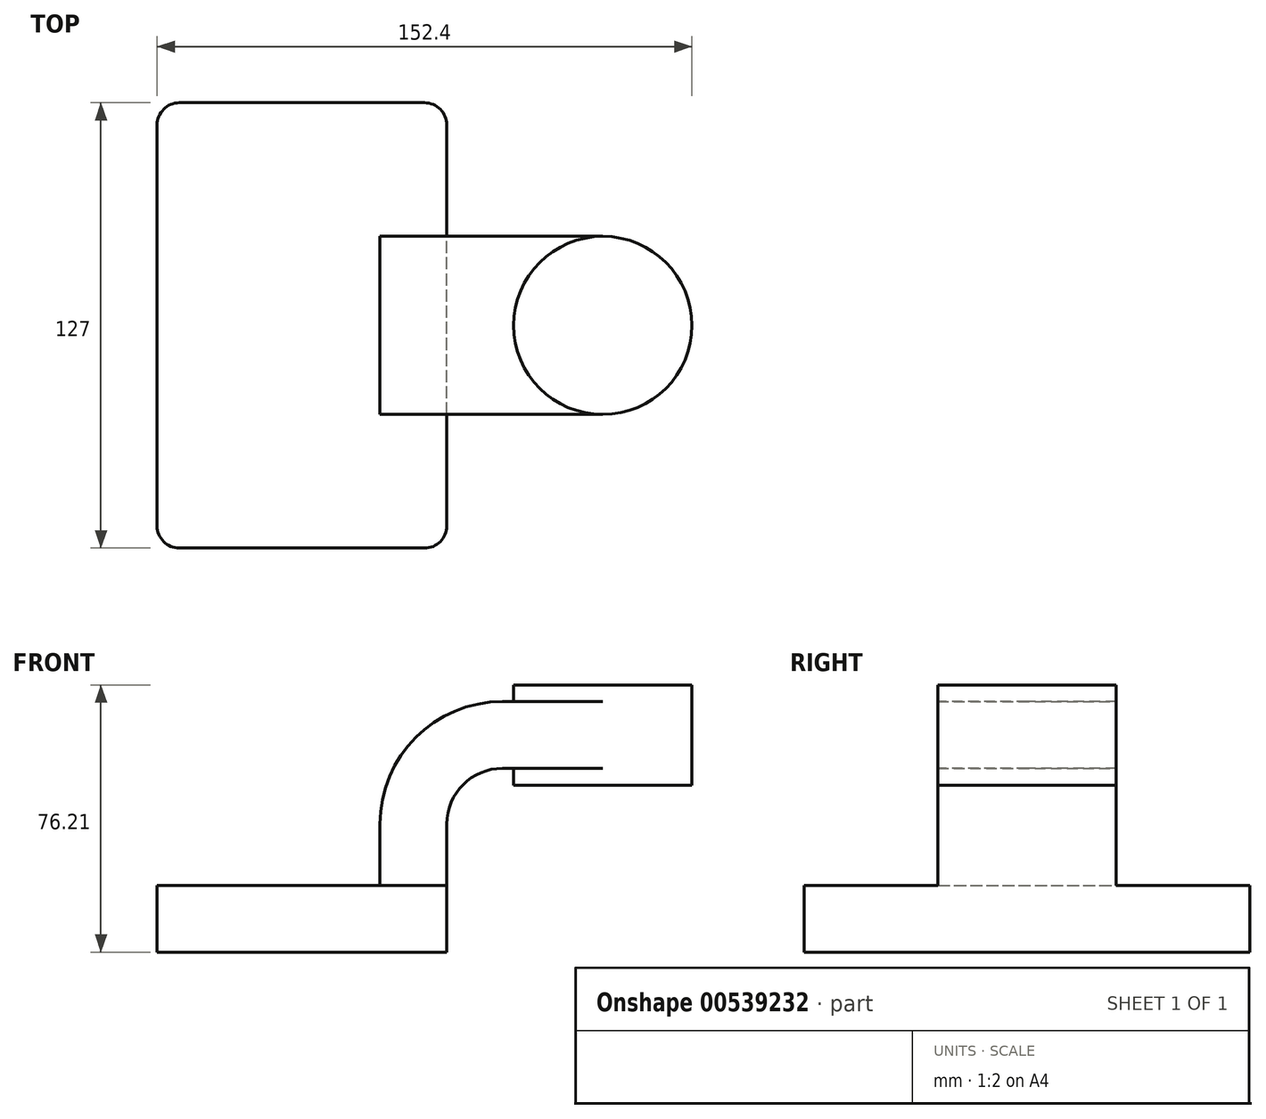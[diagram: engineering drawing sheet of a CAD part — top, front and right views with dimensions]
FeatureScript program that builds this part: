
annotation { "Feature Type Name" : "Feature", "Feature Type Description" : "" }
export const myFeature = defineFeature(function(context is Context, id is Id, definition is map)
    precondition{}
    {
        {
            var Q0;
            Q0=qCreatedBy(makeId("Front.planeOp"),FACE);
            var sketch = newSketch(context, id + "F0", { "sketchPlane" : qUnion([Q0])});
            skLineSegment(sketch, "E0.bottom", {"start": v(-41.28, -9.53) * mm, "end": v(41.28, -9.53) * mm});
            skLineSegment(sketch, "E0.top", {"start": v(-41.28, 9.53) * mm, "end": v(41.28, 9.53) * mm});
            skLineSegment(sketch, "E0.left", {"start": v(-41.28, -9.53) * mm, "end": v(-41.28, 9.53) * mm});
            skLineSegment(sketch, "E0.right", {"start": v(41.28, -9.53) * mm, "end": v(41.28, 9.53) * mm});
            skPoint(sketch, "E0.middle", {"position": v(0, 0) * mm});
            skLineSegment(sketch, "E1.bottom", {"start": v(60.33, 38.1) * mm, "end": v(111.13, 38.1) * mm});
            skLineSegment(sketch, "E1.top", {"start": v(60.33, 66.68) * mm, "end": v(111.13, 66.68) * mm});
            skLineSegment(sketch, "E1.left", {"start": v(60.33, 38.1) * mm, "end": v(60.33, 66.67) * mm});
            skLineSegment(sketch, "E1.right", {"start": v(111.13, 38.1) * mm, "end": v(111.13, 66.68) * mm});
            skPoint(sketch, "E1.middle", {"position": v(85.72, 52.39) * mm});
            skLineSegment(sketch, "E2", {"start": v(41.28, 9.53) * mm, "end": v(41.28, 27) * mm});
            skArc(sketch, "E3", {"start": v(41.28, 27) * mm, "mid": v(45.92, 38.23) * mm, "end": v(57.15, 42.88) * mm});
            skLineSegment(sketch, "E4", {"start": v(57.15, 42.88) * mm, "end": v(85.73, 42.88) * mm});
            skLineSegment(sketch, "E5.0", {"start": v(57.15, 61.93) * mm, "end": v(85.73, 61.93) * mm});
            skArc(sketch, "E5.1", {"start": v(22.22, 27) * mm, "mid": v(32.45, 51.7) * mm, "end": v(57.15, 61.93) * mm});
            skLineSegment(sketch, "E5.2", {"start": v(22.22, 9.36) * mm, "end": v(22.22, 27) * mm});
            skLineSegment(sketch, "E6", {"start": v(85.73, 38.1) * mm, "end": v(85.73, 66.68) * mm});
            skFitSpline(sketch, "E7", {"points": [v(-41.28, 9.53) * mm, v(57.15, 61.93) * mm], "startDerivative": vector(2.12, 88.03) * mm, "endDerivative": vector(105.91, -1.23) * mm});
            skSolve(sketch);
        }
        {
            var Q0;
            Q0=makeQuery(id+"F0.imprint","IMPRINT",FACE,{"disambiguationData":[TD([[makeQuery(id+"F0.imprint","IMPRINT",EDGE,{"derivedFrom":sQuery(id+"F0.wireOp",EDGE,"E0.bottom")}),1.0]])]});
            extrude(context, id + "F1", {"entities" : qUnion([Q0]), "endBound" : BoundingType.SYMMETRIC, "depth" : 127 * mm, "offsetDistance" : 25.4 * mm});
        }
        {
            var Q0;
            {var subQ1=sQuery(id+"F0.wireOp",EDGE,"E2");Q0=makeQuery(id+"F0.imprint","IMPRINT",FACE,{"disambiguationData":[TD([[makeQuery(id+"F0.imprint","IMPRINT",EDGE,{"derivedFrom":subQ1}),1.0]])]});}
            extrude(context, id + "F2", {"entities" : qUnion([Q0]), "operationType" : NewBodyOperationType.ADD, "endBound" : BoundingType.SYMMETRIC, "depth" : 50.8 * mm, "offsetDistance" : 25.4 * mm});
        }
        {
            var Q0;
            {var subQ0=sQuery(id+"F0.wireOp",EDGE,"E4");var subQ1=sQuery(id+"F0.wireOp",EDGE,"E1.left");var subQ2=makeQuery(id+"F0.imprint","INTERSECT",VERTEX,{"derivedFrom":[subQ1,subQ0]});Q0=makeQuery(id+"F0.imprint","IMPRINT",FACE,{"disambiguationData":[TD([[makeQuery(id+"F0.imprint","IMPRINT",EDGE,{"disambiguationData":[TD([[subQ2,-1.0]])],"derivedFrom":subQ1}),-1.0]])]});}
            extrude(context, id + "F3", {"entities" : qUnion([Q0]), "operationType" : NewBodyOperationType.ADD, "endBound" : BoundingType.SYMMETRIC, "depth" : 50.8 * mm, "offsetDistance" : 25.4 * mm});
        }
        {
            var Q0;
            {var subQ4=sQuery(id+"F0.wireOp",EDGE,"E5.1");Q0=makeQuery(id+"F0.imprint","IMPRINT",FACE,{"disambiguationData":[TD([[makeQuery(id+"F0.imprint","IMPRINT",EDGE,{"derivedFrom":subQ4}),1.0]])]});}
            extrude(context, id + "F4", {"entities" : qUnion([Q0]), "operationType" : NewBodyOperationType.ADD, "endBound" : BoundingType.SYMMETRIC, "depth" : 15.88 * mm, "offsetDistance" : 25.4 * mm});
        }
        {
            var Q0;
            {var subQ0=sQuery(id+"F0.wireOp",EDGE,"E1.right");Q0=makeQuery(id+"F0.imprint","IMPRINT",FACE,{"disambiguationData":[TD([[makeQuery(id+"F0.imprint","IMPRINT",EDGE,{"derivedFrom":subQ0}),1.0]])]});}
            var Q1;
            Q1=sQuery(id+"F0.wireOp",EDGE,"E6");
            revolve(context, id + "F5", {"operationType" : NewBodyOperationType.ADD, "entities" : qUnion([Q0]), "axis" : qUnion([Q1]), "revolveType" : RevolveType.FULL});
        }
        {
            var Q0;
            Q0=makeQuery(id+"F1.opExtrude","CAP_EDGE",EDGE,{"disambiguationData":[OSD([sQuery(id+"F0.wireOp",EDGE,"E0.right")])],"isStart":true});
            var Q1;
            Q1=makeQuery(id+"F1.opExtrude","CAP_EDGE",EDGE,{"disambiguationData":[OSD([sQuery(id+"F0.wireOp",EDGE,"E0.left")])],"isStart":true});
            var Q2;
            Q2=makeQuery(id+"F1.opExtrude","CAP_EDGE",EDGE,{"disambiguationData":[OSD([sQuery(id+"F0.wireOp",EDGE,"E0.left")])],"isStart":false});
            var Q3;
            Q3=makeQuery(id+"F1.opExtrude","CAP_EDGE",EDGE,{"disambiguationData":[OSD([sQuery(id+"F0.wireOp",EDGE,"E0.right")])],"isStart":false});
            fillet(context, id + "F6", {"entities" : qUnion([Q0, Q1, Q2, Q3]), "radius" : 6.35 * mm, "tangentPropagation" : true, "allowEdgeOverflow" : false});
        }
    });
